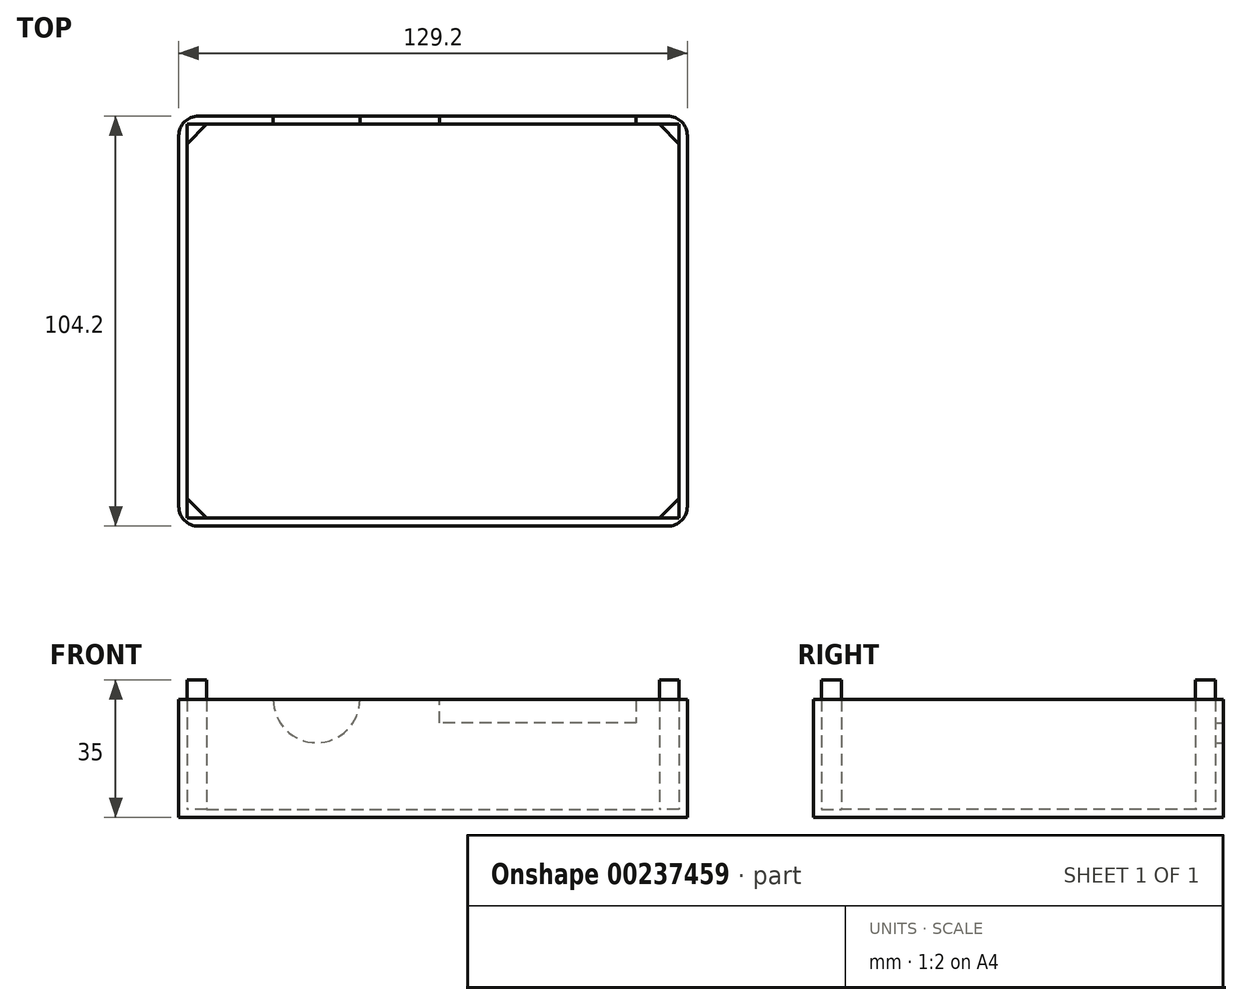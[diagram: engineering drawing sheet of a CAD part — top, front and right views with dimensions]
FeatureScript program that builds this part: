
annotation { "Feature Type Name" : "Feature", "Feature Type Description" : "" }
export const myFeature = defineFeature(function(context is Context, id is Id, definition is map)
    precondition{}
    {
        {
            var Q0;
            Q0=qCreatedBy(makeId("Top.planeOp"),FACE);
            var sketch = newSketch(context, id + "F0", { "sketchPlane" : qUnion([Q0])});
            skLineSegment(sketch, "E0", {"start": v(0, 0) * mm, "end": v(0, -100) * mm});
            skLineSegment(sketch, "E1", {"start": v(0, -100) * mm, "end": v(125, -100) * mm});
            skLineSegment(sketch, "E2", {"start": v(125, -100) * mm, "end": v(125, 0) * mm});
            skLineSegment(sketch, "E3", {"start": v(125, 0) * mm, "end": v(0, 0) * mm});
            skSolve(sketch);
        }
        {
            var Q0;
            Q0=makeQuery(id+"F0.imprint","IMPRINT",FACE,{"disambiguationData":[TD([[makeQuery(id+"F0.imprint","IMPRINT",EDGE,{"derivedFrom":sQuery(id+"F0.wireOp",EDGE,"E0")}),1.0]])]});
            extrude(context, id + "F1", {"entities" : qUnion([Q0]), "depth" : 2 * mm});
        }
        {
            var Q0;
            Q0=qCreatedBy(makeId("Top.planeOp"),FACE);
            var sketch = newSketch(context, id + "F2", { "sketchPlane" : qUnion([Q0])});
            skLineSegment(sketch, "E4", {"start": v(0, 0) * mm, "end": v(-2.1, 0) * mm, "construction": true});
            skLineSegment(sketch, "E5", {"start": v(-2.1, 0) * mm, "end": v(-2.1, 2.1) * mm, "construction": true});
            skLineSegment(sketch, "E6", {"start": v(-2.1, 2.1) * mm, "end": v(-2.1, -102.1) * mm});
            skLineSegment(sketch, "E7", {"start": v(-2.1, -102.1) * mm, "end": v(127.1, -102.1) * mm});
            skLineSegment(sketch, "E8", {"start": v(127.1, -102.1) * mm, "end": v(127.1, 2.1) * mm});
            skLineSegment(sketch, "E9", {"start": v(127.1, 2.1) * mm, "end": v(-2.1, 2.1) * mm});
            skLineSegment(sketch, "E10.0", {"start": v(125, 0) * mm, "end": v(0, 0) * mm});
            skLineSegment(sketch, "E10.1", {"start": v(0, 0) * mm, "end": v(0, -100) * mm});
            skLineSegment(sketch, "E10.2", {"start": v(0, -100) * mm, "end": v(125, -100) * mm});
            skLineSegment(sketch, "E10.3", {"start": v(125, -100) * mm, "end": v(125, 0) * mm});
            skSolve(sketch);
        }
        {
            var Q0;
            Q0 = qSketchRegion(id + "F2", true);
            extrude(context, id + "F3", {"entities" : qUnion([Q0]), "operationType" : NewBodyOperationType.ADD, "depth" : 30 * mm});
        }
        {
            var Q0;
            Q0=makeQuery(id+"F3.opExtrude","SWEPT_FACE",FACE,{"disambiguationData":[OSD([sQuery(id+"F2.wireOp",EDGE,"E9")])]});
            var sketch = newSketch(context, id + "F4", { "sketchPlane" : qUnion([Q0])});
            skLineSegment(sketch, "E11", {"start": v(2.1, 30) * mm, "end": v(-32.9, 30) * mm});
            skCircle(sketch, "E12", {"center": v(-32.9, 30) * mm, "radius": 11 * mm});
            skLineSegment(sketch, "E13", {"start": v(-127.1, 0) * mm, "end": v(-114.1, 0) * mm, "construction": true});
            skLineSegment(sketch, "E14", {"start": v(-114.1, 0) * mm, "end": v(-114.1, 24) * mm, "construction": true});
            skLineSegment(sketch, "E15", {"start": v(-114.1, 24) * mm, "end": v(-114.1, 36) * mm});
            skLineSegment(sketch, "E16", {"start": v(-114.1, 36) * mm, "end": v(-64.1, 36) * mm});
            skLineSegment(sketch, "E17", {"start": v(-64.1, 36) * mm, "end": v(-64.1, 24) * mm});
            skLineSegment(sketch, "E18", {"start": v(-64.1, 24) * mm, "end": v(-114.1, 24) * mm});
            skSolve(sketch);
        }
        {
            var Q0;
            Q0 = qSketchRegion(id + "F4", true);
            extrude(context, id + "F5", {"entities" : qUnion([Q0]), "operationType" : NewBodyOperationType.REMOVE, "oppositeDirection" : true, "depth" : 5 * mm});
        }
        {
            var Q0;
            Q0=makeQuery(id+"F1.opExtrude","CAP_FACE",FACE,{"disambiguationData":[OSD([sQuery(id+"F0.wireOp",EDGE,"E0"),sQuery(id+"F0.wireOp",EDGE,"E1"),sQuery(id+"F0.wireOp",EDGE,"E2"),sQuery(id+"F0.wireOp",EDGE,"E3")])],"isStart":false});
            var sketch = newSketch(context, id + "F6", { "sketchPlane" : qUnion([Q0])});
            skLineSegment(sketch, "E19", {"start": v(0, 0) * mm, "end": v(0, -5) * mm});
            skLineSegment(sketch, "E20", {"start": v(0, -5) * mm, "end": v(5, 0) * mm});
            skLineSegment(sketch, "E21", {"start": v(5, 0) * mm, "end": v(0, 0) * mm});
            skLineSegment(sketch, "E22", {"start": v(125, 0) * mm, "end": v(120, 0) * mm});
            skLineSegment(sketch, "E23", {"start": v(120, 0) * mm, "end": v(125, -5) * mm});
            skLineSegment(sketch, "E24", {"start": v(125, -5) * mm, "end": v(125, 0) * mm});
            skLineSegment(sketch, "E25", {"start": v(125, -100) * mm, "end": v(125, -95) * mm});
            skLineSegment(sketch, "E26", {"start": v(125, -95) * mm, "end": v(120, -100) * mm});
            skLineSegment(sketch, "E27", {"start": v(120, -100) * mm, "end": v(125, -100) * mm});
            skLineSegment(sketch, "E28", {"start": v(0, -100) * mm, "end": v(5, -100) * mm});
            skLineSegment(sketch, "E29", {"start": v(5, -100) * mm, "end": v(0, -95) * mm});
            skLineSegment(sketch, "E30", {"start": v(0, -95) * mm, "end": v(0, -100) * mm});
            skSolve(sketch);
        }
        {
            var Q0;
            Q0 = qSketchRegion(id + "F6", true);
            extrude(context, id + "F7", {"entities" : qUnion([Q0]), "operationType" : NewBodyOperationType.ADD, "depth" : 33 * mm});
        }
        {
            var Q0;
            Q0=makeQuery(id+"F3.opExtrude","SWEPT_EDGE",EDGE,{"disambiguationData":[OSD([sQuery(id+"F2.wireOp",EDGE,"E6"),sQuery(id+"F2.wireOp",EDGE,"E7")])]});
            var Q1;
            Q1=makeQuery(id+"F3.opExtrude","SWEPT_EDGE",EDGE,{"disambiguationData":[OSD([sQuery(id+"F2.wireOp",EDGE,"E7"),sQuery(id+"F2.wireOp",EDGE,"E8")])]});
            var Q2;
            Q2=makeQuery(id+"F3.opExtrude","SWEPT_EDGE",EDGE,{"disambiguationData":[OSD([sQuery(id+"F2.wireOp",EDGE,"E8"),sQuery(id+"F2.wireOp",EDGE,"E9")])]});
            var Q3;
            Q3=makeQuery(id+"F3.opExtrude","SWEPT_EDGE",EDGE,{"disambiguationData":[OSD([sQuery(id+"F2.wireOp",EDGE,"E6"),sQuery(id+"F2.wireOp",EDGE,"E9")])]});
            fillet(context, id + "F8", {"entities" : qUnion([Q0, Q1, Q2, Q3]), "radius" : 5 * mm, "tangentPropagation" : true, "allowEdgeOverflow" : false});
        }
    });
